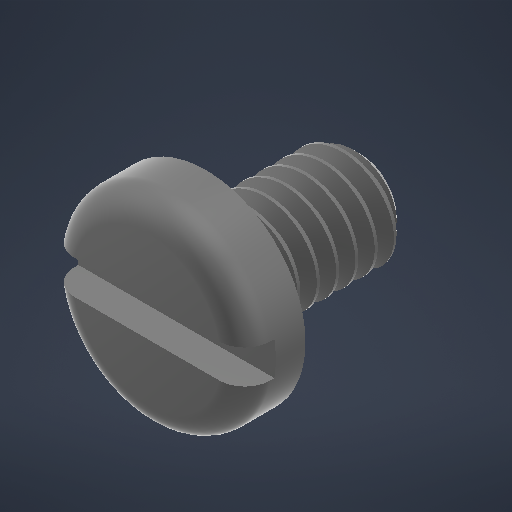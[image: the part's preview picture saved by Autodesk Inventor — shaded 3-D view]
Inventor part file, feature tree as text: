
AUTODESK INVENTOR PART (.ipt)
format: ipt  version: 2025.2 (Build 292293000, 293)  size: 412,160 bytes
history: native  units: in
note: dims shown in document units (in); Inventor stores cm internally (conversion verified against a paired STEP export)
features: other x1, extrude x1
ambient origin geometry x8: Origin, YZ Plane, XZ Plane, XY Plane, X Axis, Y Axis, Z Axis, Center Point
bodies: Solid1 (feature_tree)
feature tree (2):
  other  "Plane1"
  extrude  "Extrude15"  [1 undecoded]
note: 1 required parameter value undecoded (feature->parameter linkage not recoverable at this tier; creation-order binding heuristic only, values carry confidence <= 0.55)
